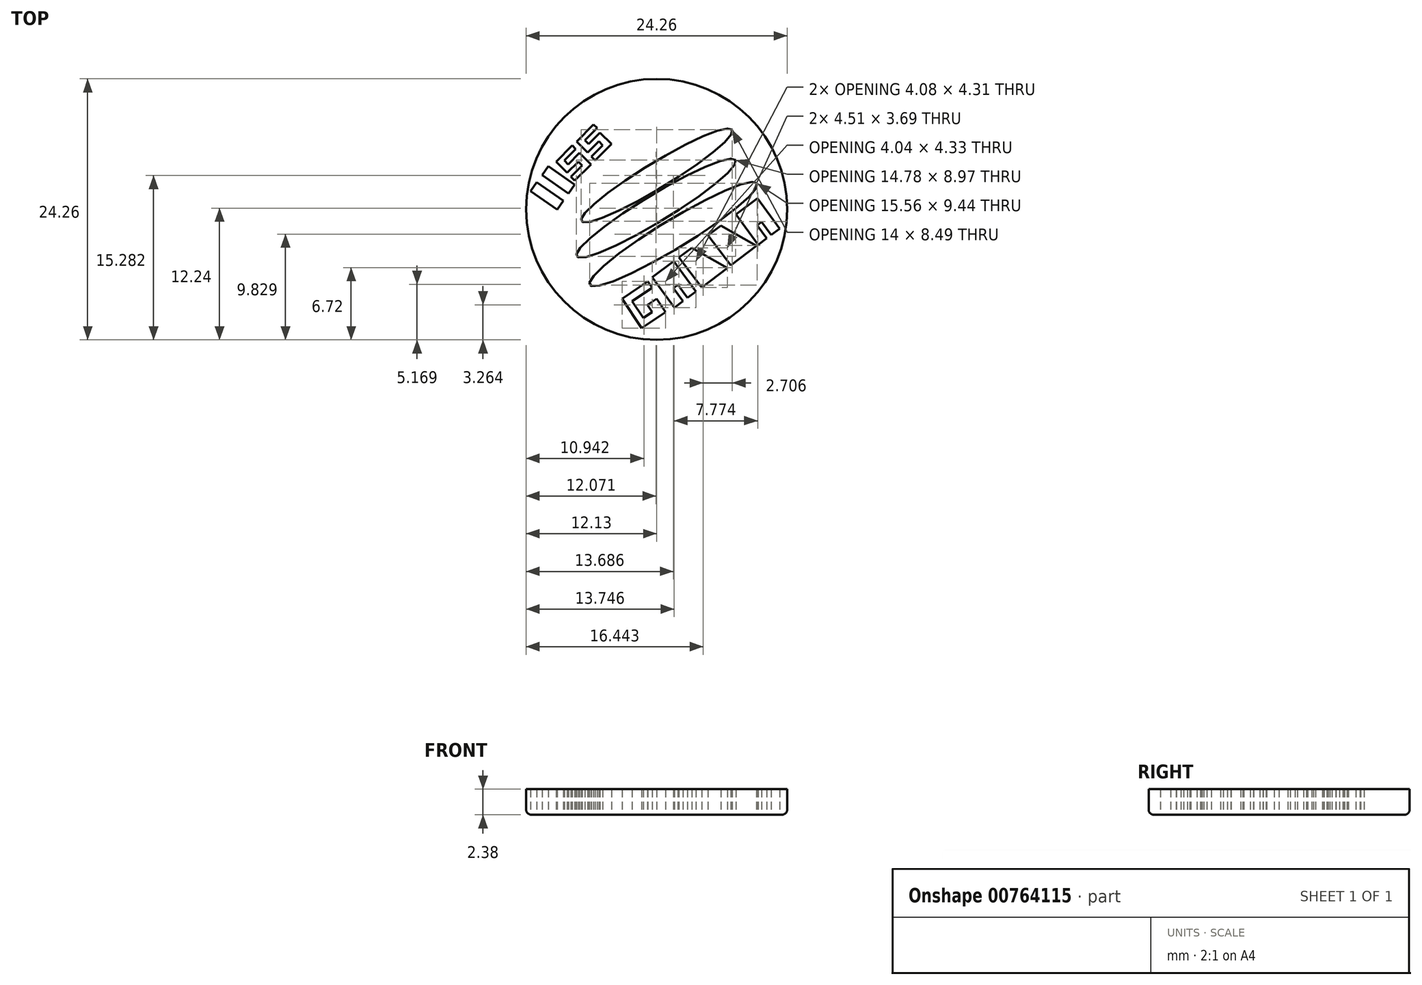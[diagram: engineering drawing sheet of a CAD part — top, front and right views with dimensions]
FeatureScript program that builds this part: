
annotation { "Feature Type Name" : "Feature", "Feature Type Description" : "" }
export const myFeature = defineFeature(function(context is Context, id is Id, definition is map)
    precondition{}
    {
        {
            var Q0;
            Q0=qCreatedBy(makeId("Top.planeOp"),FACE);
            var sketch = newSketch(context, id + "F0", { "sketchPlane" : qUnion([Q0])});
            skCircle(sketch, "E0", {"center": v(0, 0) * mm, "radius": 12.12 * mm});
            skEllipse(sketch, "E1", {"center": v(0, 3.15) * mm, "majorRadius": 8.19 * mm, "minorRadius": 1.2 * mm, "majorAxis": v(0.86, 0.52)});
            skEllipse(sketch, "E2", {"center": v(1.56, -2.3) * mm, "majorRadius": 9.1 * mm, "minorRadius": 1.32 * mm, "majorAxis": v(0.86, 0.52)});
            skEllipse(sketch, "E3", {"center": v(-0.06, 0.1) * mm, "majorRadius": 8.64 * mm, "minorRadius": 1.26 * mm, "majorAxis": v(0.86, 0.52)});
            skLineSegment(sketch, "E4", {"start": v(-10.65, 3.19) * mm, "end": v(-8.19, 1.47) * mm});
            skLineSegment(sketch, "E5", {"start": v(-10.65, 3.19) * mm, "end": v(-10.07, 4) * mm});
            skLineSegment(sketch, "E6", {"start": v(-10.07, 4) * mm, "end": v(-7.62, 2.28) * mm});
            skLineSegment(sketch, "E7", {"start": v(-7.62, 2.28) * mm, "end": v(-8.19, 1.47) * mm});
            skLineSegment(sketch, "E8", {"start": v(-5.86, 7.89) * mm, "end": v(-7.44, 6.31) * mm});
            skLineSegment(sketch, "E9", {"start": v(-6.4, 5.28) * mm, "end": v(-5.36, 6.32) * mm});
            skLineSegment(sketch, "E10", {"start": v(-6.4, 5.28) * mm, "end": v(-7.44, 6.31) * mm});
            skLineSegment(sketch, "E11", {"start": v(-5.86, 7.89) * mm, "end": v(-5.53, 7.56) * mm});
            skLineSegment(sketch, "E12", {"start": v(-5.53, 7.56) * mm, "end": v(-6.67, 6.42) * mm});
            skLineSegment(sketch, "E13", {"start": v(-6.67, 6.42) * mm, "end": v(-6.32, 6.07) * mm});
            skLineSegment(sketch, "E14", {"start": v(-5.36, 6.32) * mm, "end": v(-5.01, 5.96) * mm});
            skLineSegment(sketch, "E15", {"start": v(-5.01, 5.96) * mm, "end": v(-6.07, 4.9) * mm});
            skLineSegment(sketch, "E16", {"start": v(-6.07, 4.9) * mm, "end": v(-5.72, 4.55) * mm});
            skLineSegment(sketch, "E17", {"start": v(-6.32, 6.07) * mm, "end": v(-5.26, 7.13) * mm});
            skLineSegment(sketch, "E18", {"start": v(-5.26, 7.13) * mm, "end": v(-4.2, 6.07) * mm});
            skLineSegment(sketch, "E19", {"start": v(-4.2, 6.07) * mm, "end": v(-5.72, 4.55) * mm});
            skLineSegment(sketch, "E20", {"start": v(-11.7, 1.7) * mm, "end": v(-9.25, -0.02) * mm});
            skLineSegment(sketch, "E21", {"start": v(-11.7, 1.7) * mm, "end": v(-11.14, 2.52) * mm});
            skLineSegment(sketch, "E22", {"start": v(-11.14, 2.52) * mm, "end": v(-8.68, 0.8) * mm});
            skLineSegment(sketch, "E23", {"start": v(-8.68, 0.8) * mm, "end": v(-9.25, -0.02) * mm});
            skLineSegment(sketch, "E24", {"start": v(-7.84, 5.94) * mm, "end": v(-9.35, 4.43) * mm});
            skLineSegment(sketch, "E25", {"start": v(-8.31, 3.4) * mm, "end": v(-7.27, 4.43) * mm});
            skLineSegment(sketch, "E26", {"start": v(-8.31, 3.4) * mm, "end": v(-9.35, 4.43) * mm});
            skLineSegment(sketch, "E27", {"start": v(-7.84, 5.94) * mm, "end": v(-7.51, 5.6) * mm});
            skLineSegment(sketch, "E28", {"start": v(-7.51, 5.6) * mm, "end": v(-8.58, 4.54) * mm});
            skLineSegment(sketch, "E29", {"start": v(-8.58, 4.54) * mm, "end": v(-8.23, 4.19) * mm});
            skLineSegment(sketch, "E30", {"start": v(-7.27, 4.43) * mm, "end": v(-6.92, 4.08) * mm});
            skLineSegment(sketch, "E31", {"start": v(-6.92, 4.08) * mm, "end": v(-7.98, 3.02) * mm});
            skLineSegment(sketch, "E32", {"start": v(-7.98, 3.02) * mm, "end": v(-7.63, 2.67) * mm});
            skLineSegment(sketch, "E33", {"start": v(-8.23, 4.19) * mm, "end": v(-7.17, 5.25) * mm});
            skLineSegment(sketch, "E34", {"start": v(-7.17, 5.25) * mm, "end": v(-6.1, 4.19) * mm});
            skLineSegment(sketch, "E35", {"start": v(-6.1, 4.19) * mm, "end": v(-7.63, 2.67) * mm});
            skLineSegment(sketch, "E36", {"start": v(-0.81, -6.7) * mm, "end": v(-3.2, -8.3) * mm});
            skLineSegment(sketch, "E37", {"start": v(-3.2, -8.3) * mm, "end": v(-1.38, -11.03) * mm});
            skLineSegment(sketch, "E38", {"start": v(-1.38, -11.03) * mm, "end": v(0.83, -9.56) * mm});
            skLineSegment(sketch, "E39", {"start": v(0.83, -9.56) * mm, "end": v(0, -8.3) * mm});
            skLineSegment(sketch, "E40", {"start": v(0, -8.3) * mm, "end": v(-0.86, -8.88) * mm});
            skLineSegment(sketch, "E41", {"start": v(-0.86, -8.88) * mm, "end": v(-0.42, -9.54) * mm});
            skLineSegment(sketch, "E42", {"start": v(-0.42, -9.54) * mm, "end": v(-1.25, -10.09) * mm});
            skLineSegment(sketch, "E43", {"start": v(-1.25, -10.09) * mm, "end": v(-2.29, -8.53) * mm});
            skLineSegment(sketch, "E44", {"start": v(-2.29, -8.53) * mm, "end": v(-0.42, -7.29) * mm});
            skLineSegment(sketch, "E45", {"start": v(-0.42, -7.29) * mm, "end": v(-0.81, -6.7) * mm});
            skLineSegment(sketch, "E46", {"start": v(1.65, -9.12) * mm, "end": v(2.46, -8.52) * mm});
            skLineSegment(sketch, "E47", {"start": v(2.46, -8.52) * mm, "end": v(1.56, -7.3) * mm});
            skLineSegment(sketch, "E48", {"start": v(1.56, -7.3) * mm, "end": v(1.96, -7) * mm});
            skLineSegment(sketch, "E49", {"start": v(1.96, -7) * mm, "end": v(2.85, -8.22) * mm});
            skLineSegment(sketch, "E50", {"start": v(2.85, -8.22) * mm, "end": v(3.66, -7.62) * mm});
            skLineSegment(sketch, "E51", {"start": v(3.66, -7.62) * mm, "end": v(1.58, -4.8) * mm});
            skLineSegment(sketch, "E52", {"start": v(1.65, -9.12) * mm, "end": v(-0.42, -6.3) * mm});
            skLineSegment(sketch, "E53", {"start": v(-0.42, -6.3) * mm, "end": v(1.58, -4.8) * mm});
            skLineSegment(sketch, "E54", {"start": v(0.92, -6.91) * mm, "end": v(1.72, -6.31) * mm});
            skLineSegment(sketch, "E55", {"start": v(1.72, -6.31) * mm, "end": v(1.41, -5.91) * mm});
            skLineSegment(sketch, "E56", {"start": v(1.41, -5.91) * mm, "end": v(0.62, -6.52) * mm});
            skLineSegment(sketch, "E57", {"start": v(0.62, -6.52) * mm, "end": v(0.92, -6.91) * mm});
            skLineSegment(sketch, "E58", {"start": v(4.18, -7.26) * mm, "end": v(2.06, -4.47) * mm});
            skLineSegment(sketch, "E59", {"start": v(2.06, -4.47) * mm, "end": v(3.25, -3.56) * mm});
            skLineSegment(sketch, "E60", {"start": v(4.18, -7.26) * mm, "end": v(6.57, -5.44) * mm});
            skLineSegment(sketch, "E61", {"start": v(6.57, -5.44) * mm, "end": v(3.25, -3.56) * mm});
            skLineSegment(sketch, "E62", {"start": v(4.2, -6.22) * mm, "end": v(5.24, -5.43) * mm});
            skLineSegment(sketch, "E63", {"start": v(4.2, -6.22) * mm, "end": v(3.3, -5.02) * mm});
            skLineSegment(sketch, "E64", {"start": v(3.3, -5.02) * mm, "end": v(3.7, -4.72) * mm});
            skLineSegment(sketch, "E65", {"start": v(3.7, -4.72) * mm, "end": v(5.24, -5.43) * mm});
            skLineSegment(sketch, "E66", {"start": v(6.88, -5.2) * mm, "end": v(4.77, -2.4) * mm});
            skLineSegment(sketch, "E67", {"start": v(4.77, -2.4) * mm, "end": v(5.96, -1.5) * mm});
            skLineSegment(sketch, "E68", {"start": v(6.88, -5.2) * mm, "end": v(9.27, -3.37) * mm});
            skLineSegment(sketch, "E69", {"start": v(9.27, -3.37) * mm, "end": v(5.96, -1.5) * mm});
            skLineSegment(sketch, "E70", {"start": v(6.92, -4.17) * mm, "end": v(7.97, -3.38) * mm});
            skLineSegment(sketch, "E71", {"start": v(6.92, -4.17) * mm, "end": v(6, -2.96) * mm});
            skLineSegment(sketch, "E72", {"start": v(6, -2.96) * mm, "end": v(6.4, -2.65) * mm});
            skLineSegment(sketch, "E73", {"start": v(6.4, -2.65) * mm, "end": v(7.97, -3.38) * mm});
            skLineSegment(sketch, "E74", {"start": v(9.43, -3.28) * mm, "end": v(10.23, -2.68) * mm});
            skLineSegment(sketch, "E75", {"start": v(10.23, -2.68) * mm, "end": v(9.33, -1.47) * mm});
            skLineSegment(sketch, "E76", {"start": v(9.33, -1.47) * mm, "end": v(9.74, -1.17) * mm});
            skLineSegment(sketch, "E77", {"start": v(9.74, -1.17) * mm, "end": v(10.63, -2.38) * mm});
            skLineSegment(sketch, "E78", {"start": v(10.63, -2.38) * mm, "end": v(11.43, -1.78) * mm});
            skLineSegment(sketch, "E79", {"start": v(11.43, -1.78) * mm, "end": v(9.36, 1.03) * mm});
            skLineSegment(sketch, "E80", {"start": v(9.43, -3.28) * mm, "end": v(7.35, -0.46) * mm});
            skLineSegment(sketch, "E81", {"start": v(7.35, -0.46) * mm, "end": v(9.36, 1.03) * mm});
            skLineSegment(sketch, "E82", {"start": v(8.7, -1.08) * mm, "end": v(9.49, -0.47) * mm});
            skLineSegment(sketch, "E83", {"start": v(9.49, -0.47) * mm, "end": v(9.19, -0.07) * mm});
            skLineSegment(sketch, "E84", {"start": v(9.19, -0.07) * mm, "end": v(8.4, -0.68) * mm});
            skLineSegment(sketch, "E85", {"start": v(8.4, -0.68) * mm, "end": v(8.7, -1.08) * mm});
            skSolve(sketch);
        }
        {
            assignVariable(context, id + "F1", {"name" : "Spess", "anyValue" : 2.38});
        }
        {
            var Q0;
            Q0=makeQuery(id+"F0.imprint","IMPRINT",FACE,{"disambiguationData":[TD([[makeQuery(id+"F0.imprint","IMPRINT",EDGE,{"derivedFrom":sQuery(id+"F0.wireOp",EDGE,"E0")}),1.0]])]});
            extrude(context, id + "F2", {"entities" : qUnion([Q0]), "depth" : (getVariable(context, 'Spess')) * mm, "offsetDistance" : 25 * mm});
        }
        {
            var Q0;
            Q0=makeQuery(id+"F2.opExtrude","CAP_EDGE",EDGE,{"disambiguationData":[OSD([sQuery(id+"F0.wireOp",EDGE,"E0")])],"isStart":true});
            fillet(context, id + "F3", {"entities" : qUnion([Q0]), "radius" : .5 * mm, "tangentPropagation" : true, "allowEdgeOverflow" : false});
        }
    });
